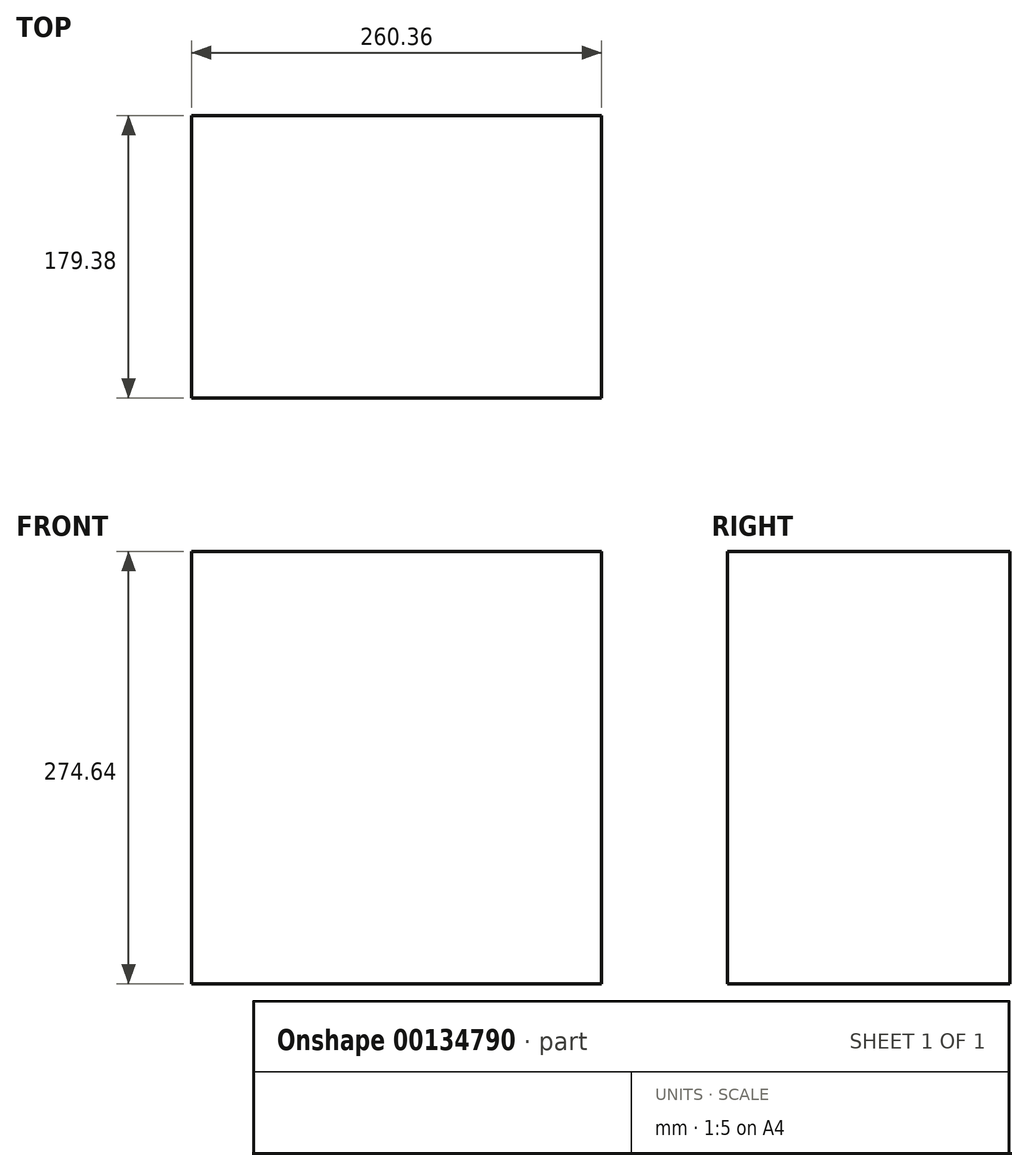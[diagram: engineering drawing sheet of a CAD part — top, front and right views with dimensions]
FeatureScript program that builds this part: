
annotation { "Feature Type Name" : "Feature", "Feature Type Description" : "" }
export const myFeature = defineFeature(function(context is Context, id is Id, definition is map)
    precondition{}
    {
        {
            var Q0;
            Q0=qCreatedBy(makeId("Top.planeOp"),FACE);
            var sketch = newSketch(context, id + "F0", { "sketchPlane" : qUnion([Q0])});
            skLineSegment(sketch, "E0.bottom", {"start": v(130.18, 89.7) * mm, "end": v(-130.18, 89.7) * mm});
            skLineSegment(sketch, "E0.top", {"start": v(130.18, -89.7) * mm, "end": v(-130.18, -89.7) * mm});
            skLineSegment(sketch, "E0.left", {"start": v(130.18, 89.7) * mm, "end": v(130.18, -89.7) * mm});
            skLineSegment(sketch, "E0.right", {"start": v(-130.18, 89.7) * mm, "end": v(-130.18, -89.7) * mm});
            skPoint(sketch, "E0.middle", {"position": v(0, 0) * mm});
            skSolve(sketch);
        }
        {
            var Q0;
            Q0=makeQuery(id+"F0.imprint","IMPRINT",FACE,{"disambiguationData":[TD([[makeQuery(id+"F0.imprint","IMPRINT",EDGE,{"derivedFrom":sQuery(id+"F0.wireOp",EDGE,"E0.bottom")}),1.0]])]});
            extrude(context, id + "F1", {"entities" : qUnion([Q0]), "depth" : 274.64 * mm});
        }
    });
